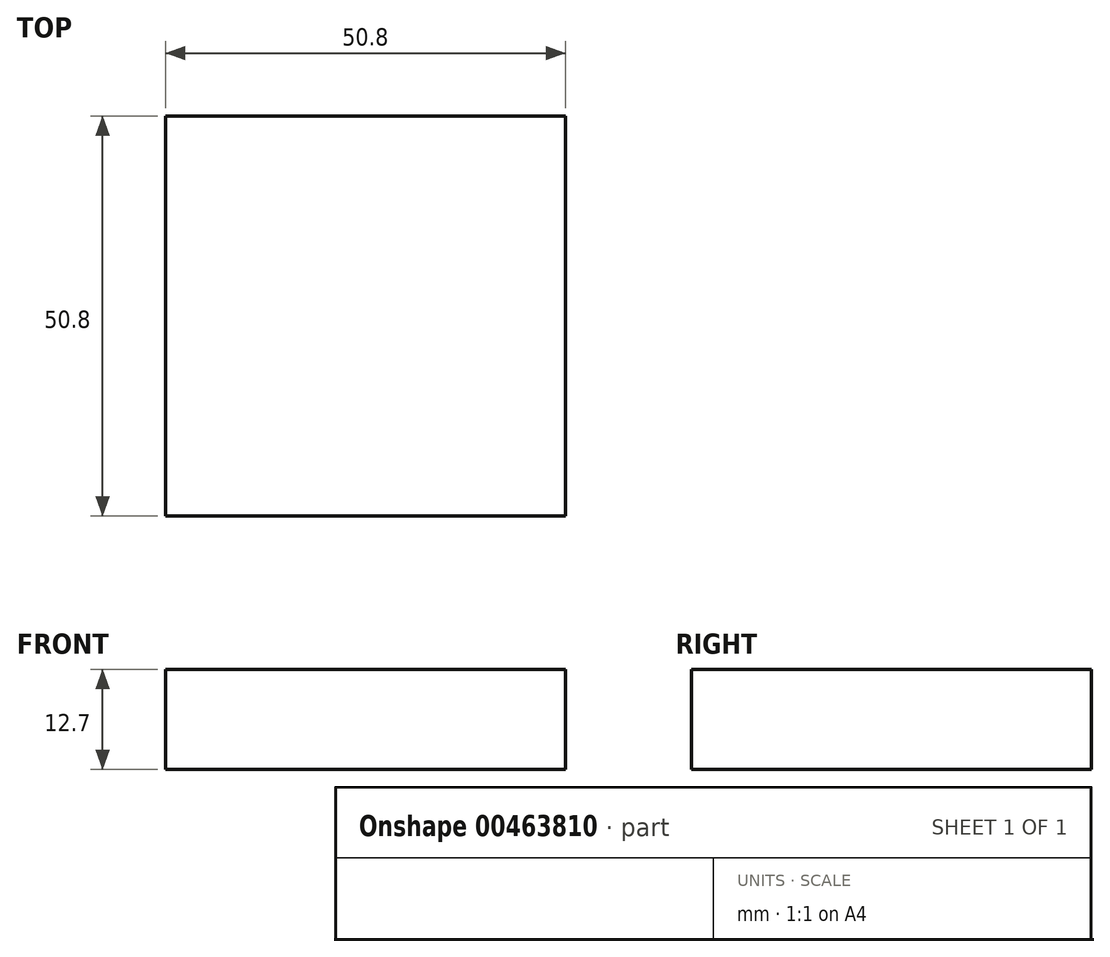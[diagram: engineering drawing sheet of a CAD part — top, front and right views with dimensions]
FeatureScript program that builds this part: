
annotation { "Feature Type Name" : "Feature", "Feature Type Description" : "" }
export const myFeature = defineFeature(function(context is Context, id is Id, definition is map)
    precondition{}
    {
        {
            var Q0;
            Q0=qCreatedBy(makeId("Front.planeOp"),FACE);
            var sketch = newSketch(context, id + "F0", { "sketchPlane" : qUnion([Q0])});
            skLineSegment(sketch, "E0.bottom", {"start": v(-33.54, 15.27) * mm, "end": v(17.26, 15.27) * mm});
            skLineSegment(sketch, "E0.top", {"start": v(-33.54, 2.57) * mm, "end": v(17.26, 2.57) * mm});
            skLineSegment(sketch, "E0.left", {"start": v(-33.54, 15.27) * mm, "end": v(-33.54, 2.57) * mm});
            skLineSegment(sketch, "E0.right", {"start": v(17.26, 15.27) * mm, "end": v(17.26, 2.57) * mm});
            skSolve(sketch);
        }
        {
            var Q0;
            Q0=makeQuery(id+"F0.imprint","IMPRINT",FACE,{"disambiguationData":[TD([[makeQuery(id+"F0.imprint","IMPRINT",EDGE,{"derivedFrom":sQuery(id+"F0.wireOp",EDGE,"E0.bottom")}),-1.0]])]});
            extrude(context, id + "F1", {"entities" : qUnion([Q0]), "depth" : 50.8 * mm});
        }
    });
